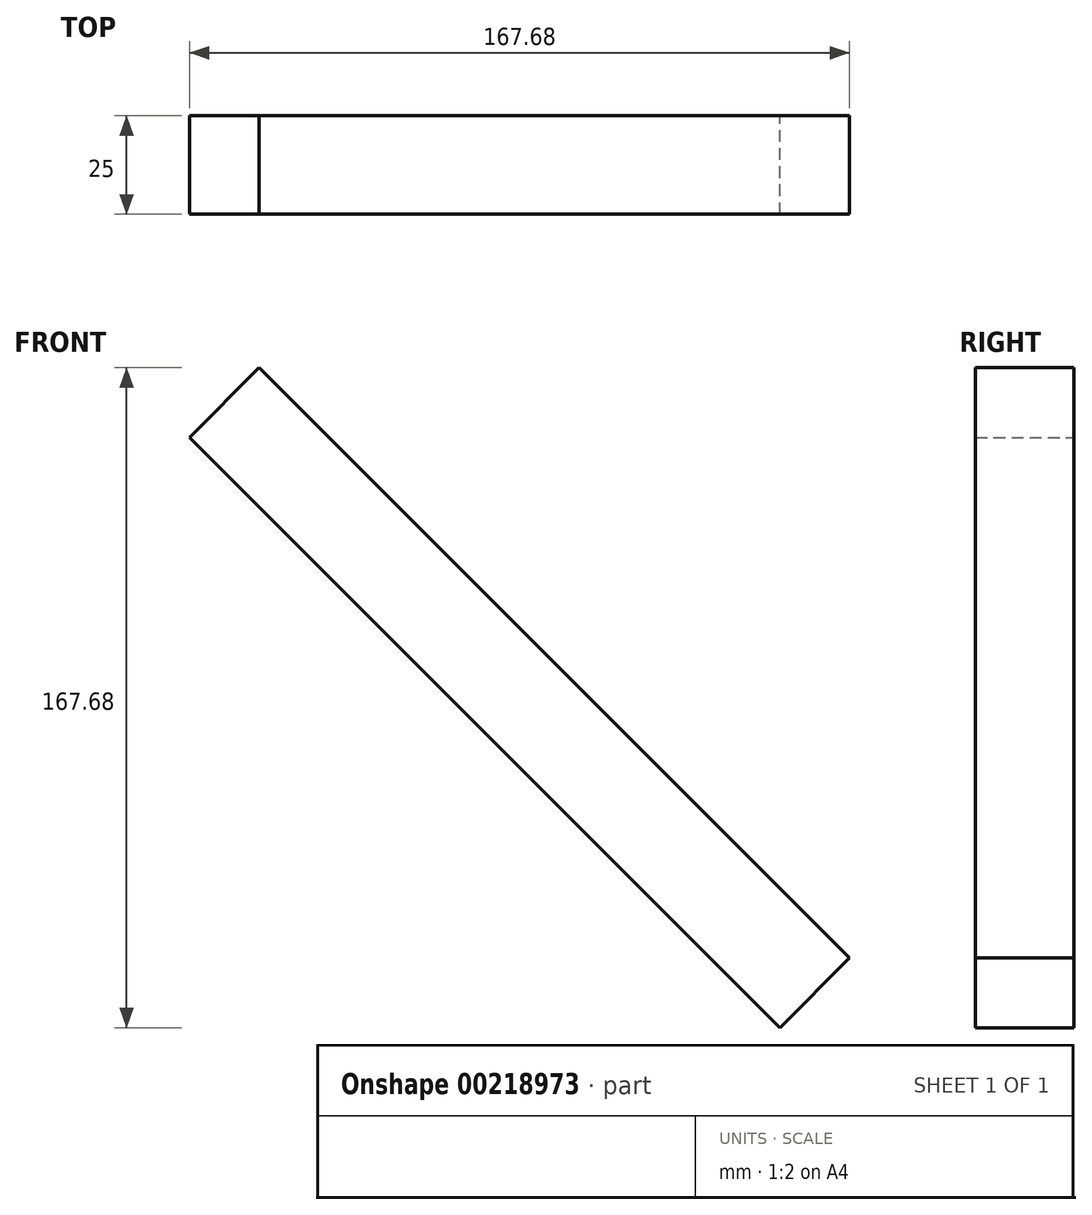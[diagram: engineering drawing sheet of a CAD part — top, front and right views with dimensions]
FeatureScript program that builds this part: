
annotation { "Feature Type Name" : "Feature", "Feature Type Description" : "" }
export const myFeature = defineFeature(function(context is Context, id is Id, definition is map)
    precondition{}
    {
        {
            var Q0;
            Q0=qCreatedBy(makeId("Front.planeOp"), FACE);
            var sketch = newSketch(context, id + "F0", { "sketchPlane" : qUnion([Q0])});
            skLineSegment(sketch, "E0", {"start": v(-150, 150) * mm, "end": v(0, 0) * mm});
            skLineSegment(sketch, "E1", {"start": v(-150, 150) * mm, "end": v(-132.32, 167.68) * mm});
            skLineSegment(sketch, "E2", {"start": v(0, 0) * mm, "end": v(17.68, 17.68) * mm});
            skLineSegment(sketch, "E3", {"start": v(17.68, 17.68) * mm, "end": v(-132.32, 167.68) * mm});
            skSolve(sketch);
        }
        {
            var Q0;
            Q0 = qSketchRegion(id + "F0", true);
            extrude(context, id + "F1", {"entities" : qUnion([Q0]), "depth" : 25 * mm, "offsetDistance" : 25 * mm});
        }
    });
